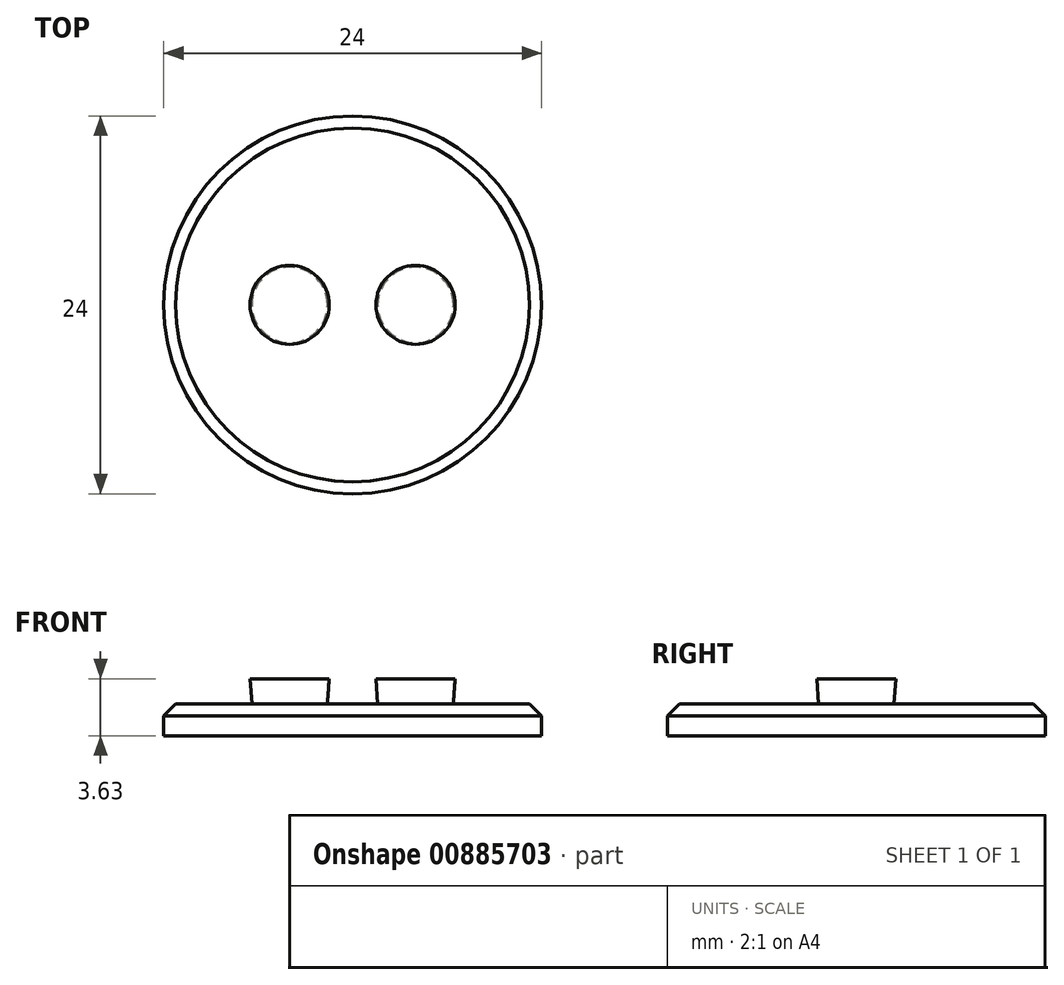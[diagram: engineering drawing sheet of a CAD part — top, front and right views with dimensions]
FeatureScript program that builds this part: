
annotation { "Feature Type Name" : "Feature", "Feature Type Description" : "" }
export const myFeature = defineFeature(function(context is Context, id is Id, definition is map)
    precondition{}
    {
        {
            var Q0;
            Q0=qCreatedBy(makeId("Top.planeOp"),FACE);
            var sketch = newSketch(context, id + "F0", { "sketchPlane" : qUnion([Q0])});
            skCircle(sketch, "E0", {"center": v(0, 0) * mm, "radius": 12 * mm});
            skSolve(sketch);
        }
        {
            var Q0;
            Q0 = qSketchRegion(id + "F0", true);
            extrude(context, id + "F1", {"entities" : qUnion([Q0]), "depth" : 2.03 * mm, "offsetDistance" : 25.4 * mm});
        }
        {
            var Q0;
            Q0=makeQuery(id+"F1.opExtrude","CAP_EDGE",EDGE,{"disambiguationData":[OSD([sQuery(id+"F0.wireOp",EDGE,"E0")])],"isStart":false});
            chamfer(context, id + "F2", {"entities" : qUnion([Q0]), "width" : 0.76 * mm, "tangentPropagation" : true});
        }
        {
            var Q0;
            Q0=makeQuery(id+"F1.opExtrude","CAP_FACE",FACE,{"disambiguationData":[OSD([sQuery(id+"F0.wireOp",EDGE,"E0")])],"isStart":false});
            var sketch = newSketch(context, id + "F3", { "sketchPlane" : qUnion([Q0])});
            skCircle(sketch, "E1", {"center": v(4, 0) * mm, "radius": 2.4 * mm});
            skCircle(sketch, "E2", {"center": v(-4, 0) * mm, "radius": 2.4 * mm});
            skLineSegment(sketch, "E3", {"start": v(4, 0) * mm, "end": v(-4, 0) * mm, "construction": true});
            skSolve(sketch);
        }
        {
            var Q0;
            Q0 = qSketchRegion(id + "F3", true);
            extrude(context, id + "F4", {"entities" : qUnion([Q0]), "operationType" : NewBodyOperationType.ADD, "depth" : 1.6 * mm, "offsetDistance" : 25.4 * mm, "hasDraft" : true, "draftAngle" : 4 * degree});
        }
    });
